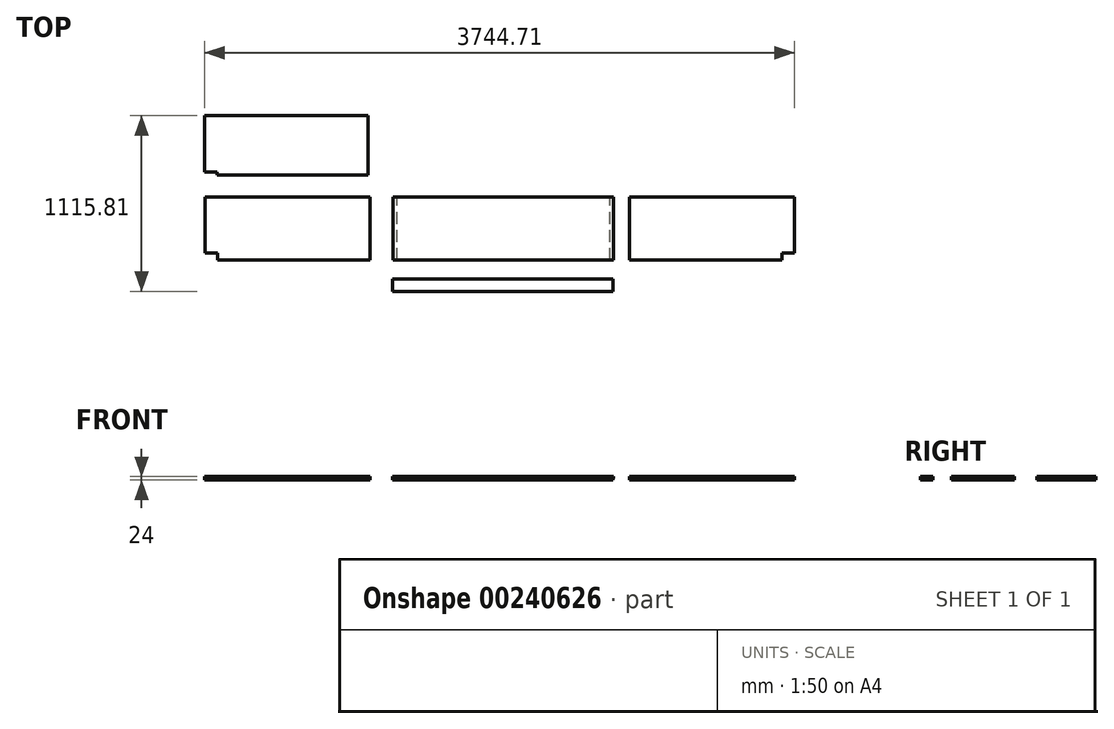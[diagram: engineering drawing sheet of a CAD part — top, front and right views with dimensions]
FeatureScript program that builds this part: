
annotation { "Feature Type Name" : "Feature", "Feature Type Description" : "" }
export const myFeature = defineFeature(function(context is Context, id is Id, definition is map)
    precondition{}
    {
        {
            assignVariable(context, id + "F0", {"name" : "Lev_pak", "anyValue" : 24});
        }
        {
            var Q0;
            Q0=qCreatedBy(makeId("Top.planeOp"),FACE);
            var sketch = newSketch(context, id + "F1", { "sketchPlane" : qUnion([Q0])});
            skLineSegment(sketch, "E0.bottom", {"start": v(-1316.9, 370.44) * mm, "end": v(83.1, 370.44) * mm});
            skLineSegment(sketch, "E0.top", {"start": v(-1316.9, -29.56) * mm, "end": v(83.1, -29.56) * mm});
            skLineSegment(sketch, "E0.left", {"start": v(-1316.9, 370.44) * mm, "end": v(-1316.9, -29.56) * mm});
            skLineSegment(sketch, "E0.right", {"start": v(83.1, 370.44) * mm, "end": v(83.1, -29.56) * mm});
            skSolve(sketch);
        }
        {
            var Q0;
            Q0=makeQuery(id+"F1.imprint","IMPRINT",FACE,{"disambiguationData":[TD([[makeQuery(id+"F1.imprint","IMPRINT",EDGE,{"derivedFrom":sQuery(id+"F1.wireOp",EDGE,"E0.bottom")}),-1.0]])]});
            extrude(context, id + "F2", {"entities" : qUnion([Q0]), "depth" : (getVariable(context, 'Lev_pak')) * mm});
        }
        {
            var Q0;
            Q0=makeQuery(id+"F2.opExtrude","CAP_FACE",FACE,{"disambiguationData":[OSD([sQuery(id+"F1.wireOp",EDGE,"E0.bottom"),sQuery(id+"F1.wireOp",EDGE,"E0.top"),sQuery(id+"F1.wireOp",EDGE,"E0.left"),sQuery(id+"F1.wireOp",EDGE,"E0.right")])],"isStart":true});
            var sketch = newSketch(context, id + "F3", { "sketchPlane" : qUnion([Q0])});
            skLineSegment(sketch, "E1.bottom", {"start": v(-1316.9, 29.56) * mm, "end": v(-1292.9, 29.56) * mm});
            skLineSegment(sketch, "E1.top", {"start": v(-1316.9, -370.44) * mm, "end": v(-1292.9, -370.44) * mm});
            skLineSegment(sketch, "E1.left", {"start": v(-1316.9, 29.56) * mm, "end": v(-1316.9, -370.44) * mm});
            skLineSegment(sketch, "E1.right", {"start": v(-1292.9, 29.56) * mm, "end": v(-1292.9, -370.44) * mm});
            skLineSegment(sketch, "E2.bottom", {"start": v(83.1, 29.56) * mm, "end": v(59.1, 29.56) * mm});
            skLineSegment(sketch, "E2.top", {"start": v(83.1, -370.44) * mm, "end": v(59.1, -370.44) * mm});
            skLineSegment(sketch, "E2.left", {"start": v(83.1, 29.56) * mm, "end": v(83.1, -370.44) * mm});
            skLineSegment(sketch, "E2.right", {"start": v(59.1, 29.56) * mm, "end": v(59.1, -370.44) * mm});
            skSolve(sketch);
        }
        {
            var Q0;
            Q0 = qSketchRegion(id + "F3", true);
            extrude(context, id + "F4", {"entities" : qUnion([Q0]), "operationType" : NewBodyOperationType.REMOVE, "oppositeDirection" : true, "depth" : 12 * mm});
        }
        {
            var Q0;
            Q0=qCreatedBy(makeId("Top.planeOp"),FACE);
            var sketch = newSketch(context, id + "F5", { "sketchPlane" : qUnion([Q0])});
            skLineSegment(sketch, "E3.bottom", {"start": v(182.45, 370.44) * mm, "end": v(1230.45, 370.44) * mm});
            skLineSegment(sketch, "E3.top", {"start": v(182.45, -29.56) * mm, "end": v(1150.45, -29.56) * mm});
            skLineSegment(sketch, "E3.left", {"start": v(182.45, 370.44) * mm, "end": v(182.45, -29.56) * mm});
            skLineSegment(sketch, "E3.right", {"start": v(1230.45, 370.44) * mm, "end": v(1230.45, 14.44) * mm});
            skLineSegment(sketch, "E4", {"start": v(1230.45, 14.44) * mm, "end": v(1150.45, 14.44) * mm});
            skLineSegment(sketch, "E5", {"start": v(1150.45, 14.44) * mm, "end": v(1150.45, -29.56) * mm});
            skSolve(sketch);
        }
        {
            var Q0;
            Q0 = qSketchRegion(id + "F5", true);
            extrude(context, id + "F6", {"entities" : qUnion([Q0]), "depth" : 24 * mm});
        }
        {
            var Q0;
            Q0=qCreatedBy(makeId("Top.planeOp"),FACE);
            var sketch = newSketch(context, id + "F7", { "sketchPlane" : qUnion([Q0])});
            skLineSegment(sketch, "E6.bottom", {"start": v(-1462.88, 370.44) * mm, "end": v(-2510.88, 370.44) * mm});
            skLineSegment(sketch, "E6.top", {"start": v(-1462.88, -29.56) * mm, "end": v(-2430.88, -29.56) * mm});
            skLineSegment(sketch, "E6.left", {"start": v(-1462.88, 370.44) * mm, "end": v(-1462.88, -29.56) * mm});
            skLineSegment(sketch, "E6.right", {"start": v(-2510.88, 370.44) * mm, "end": v(-2510.88, 14.44) * mm});
            skLineSegment(sketch, "E7", {"start": v(-2510.88, 14.44) * mm, "end": v(-2430.88, 14.44) * mm});
            skLineSegment(sketch, "E8", {"start": v(-2430.88, 14.44) * mm, "end": v(-2430.88, -29.56) * mm});
            skSolve(sketch);
        }
        {
            var Q0;
            Q0=makeQuery(id+"F7.imprint","IMPRINT",FACE,{"disambiguationData":[TD([[makeQuery(id+"F7.imprint","IMPRINT",EDGE,{"derivedFrom":sQuery(id+"F7.wireOp",EDGE,"E6.bottom")}),1.0]])]});
            extrude(context, id + "F8", {"entities" : qUnion([Q0]), "depth" : 24 * mm});
        }
        {
            var Q0;
            Q0=qCreatedBy(makeId("Top.planeOp"),FACE);
            var sketch = newSketch(context, id + "F9", { "sketchPlane" : qUnion([Q0])});
            skLineSegment(sketch, "E9.bottom", {"start": v(-1478.26, 511.04) * mm, "end": v(-2434.26, 511.04) * mm});
            skLineSegment(sketch, "E9.top", {"start": v(-1478.26, 887.04) * mm, "end": v(-2514.26, 887.04) * mm});
            skLineSegment(sketch, "E9.left", {"start": v(-1478.26, 511.04) * mm, "end": v(-1478.26, 887.04) * mm});
            skLineSegment(sketch, "E9.right", {"start": v(-2514.26, 531.04) * mm, "end": v(-2514.26, 887.04) * mm});
            skLineSegment(sketch, "E10", {"start": v(-2514.26, 531.04) * mm, "end": v(-2434.26, 531.04) * mm});
            skLineSegment(sketch, "E11", {"start": v(-2434.26, 531.04) * mm, "end": v(-2434.26, 511.04) * mm});
            skSolve(sketch);
        }
        {
            var Q0;
            Q0=makeQuery(id+"F9.imprint","IMPRINT",FACE,{"disambiguationData":[TD([[makeQuery(id+"F9.imprint","IMPRINT",EDGE,{"derivedFrom":sQuery(id+"F9.wireOp",EDGE,"E9.bottom")}),-1.0]])]});
            extrude(context, id + "F10", {"entities" : qUnion([Q0]), "depth" : 24 * mm});
        }
        {
            var Q0;
            Q0=qCreatedBy(makeId("Top.planeOp"),FACE);
            var sketch = newSketch(context, id + "F11", { "sketchPlane" : qUnion([Q0])});
            skLineSegment(sketch, "E12.bottom", {"start": v(-1320.48, -148.77) * mm, "end": v(79.52, -148.77) * mm});
            skLineSegment(sketch, "E12.top", {"start": v(-1320.48, -228.77) * mm, "end": v(79.52, -228.77) * mm});
            skLineSegment(sketch, "E12.left", {"start": v(-1320.48, -148.77) * mm, "end": v(-1320.48, -228.77) * mm});
            skLineSegment(sketch, "E12.right", {"start": v(79.52, -148.77) * mm, "end": v(79.52, -228.77) * mm});
            skSolve(sketch);
        }
        {
            var Q0;
            Q0=makeQuery(id+"F11.imprint","IMPRINT",FACE,{"disambiguationData":[TD([[makeQuery(id+"F11.imprint","IMPRINT",EDGE,{"derivedFrom":sQuery(id+"F11.wireOp",EDGE,"E12.bottom")}),-1.0]])]});
            extrude(context, id + "F12", {"entities" : qUnion([Q0]), "depth" : 24 * mm});
        }
    });
